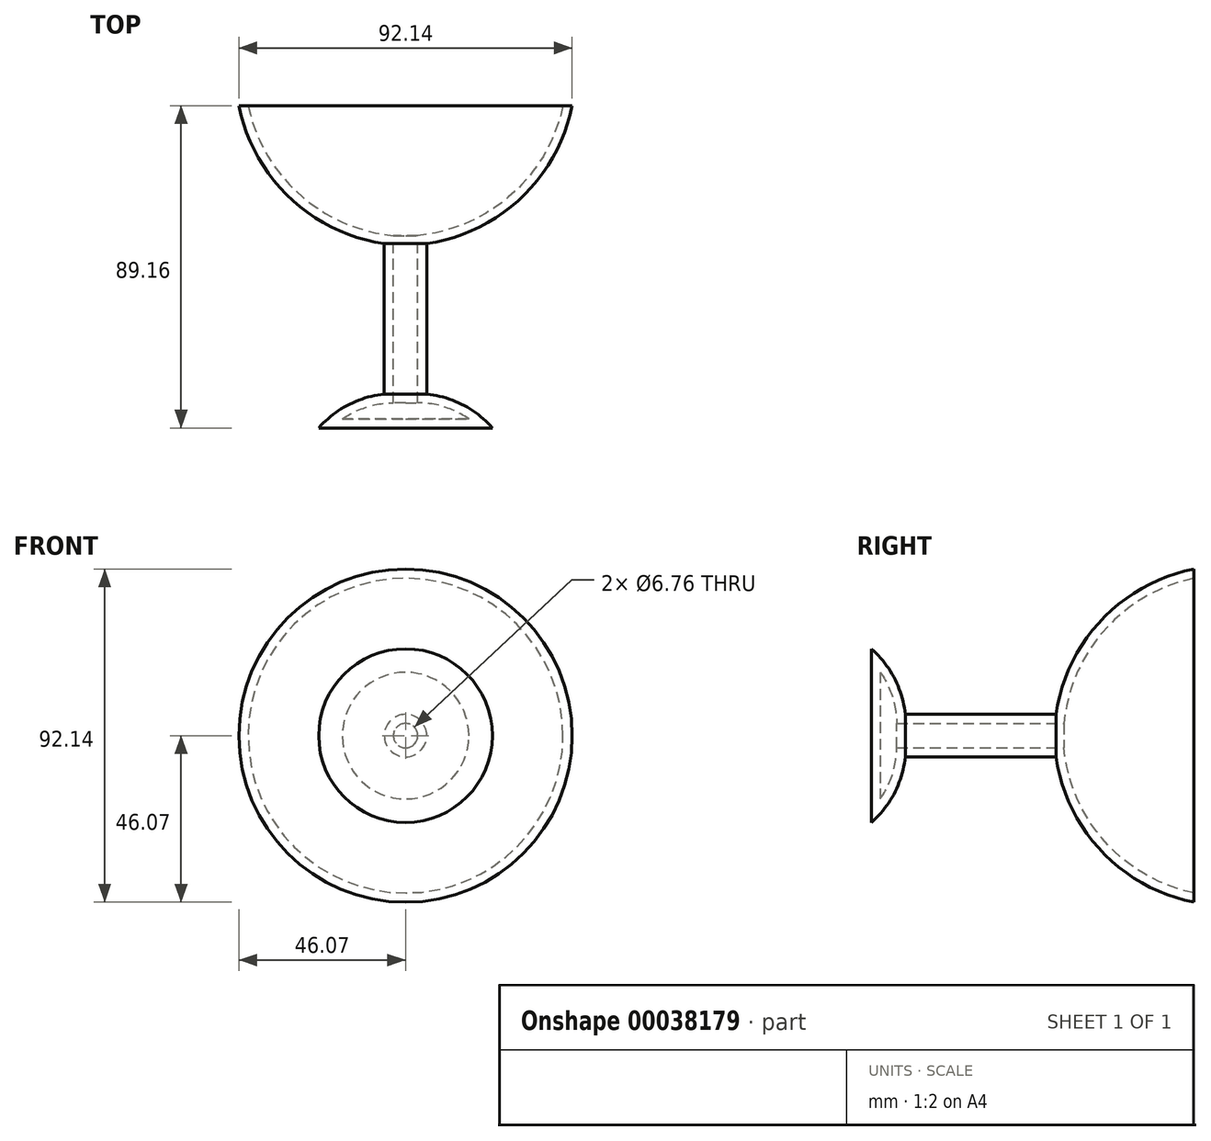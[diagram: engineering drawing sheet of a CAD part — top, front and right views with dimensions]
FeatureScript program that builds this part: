
annotation { "Feature Type Name" : "Feature", "Feature Type Description" : "" }
export const myFeature = defineFeature(function(context is Context, id is Id, definition is map)
    precondition{}
    {
        {
            var Q0;
            Q0=qCreatedBy(makeId("Top.planeOp"),FACE);
            var sketch = newSketch(context, id + "F0", { "sketchPlane" : qUnion([Q0])});
            skLineSegment(sketch, "E0", {"start": v(0, 40.65) * mm, "end": v(0, -48.5) * mm});
            skLineSegment(sketch, "E1", {"start": v(0, -48.5) * mm, "end": v(24.01, -48.5) * mm});
            skLineSegment(sketch, "E2", {"start": v(0, 40.65) * mm, "end": v(46.07, 40.65) * mm});
            skLineSegment(sketch, "E3", {"start": v(5.88, 2.52) * mm, "end": v(5.88, -39.14) * mm});
            skArc(sketch, "E4", {"start": v(5.88, 2.52) * mm, "mid": v(32.04, 15.2) * mm, "end": v(46.07, 40.65) * mm});
            skArc(sketch, "E5", {"start": v(24.01, -48.5) * mm, "mid": v(15.84, -42.1) * mm, "end": v(5.88, -39.14) * mm});
            skSolve(sketch);
        }
        {
            var Q0;
            Q0=makeQuery(id+"F0.imprint","IMPRINT",FACE,{"disambiguationData":[TD([[makeQuery(id+"F0.imprint","IMPRINT",EDGE,{"derivedFrom":sQuery(id+"F0.wireOp",EDGE,"E0")}),1.0]])]});
            var Q1;
            Q1=sQuery(id+"F0.wireOp",EDGE,"E0");
            revolve(context, id + "F1", {"entities" : qUnion([Q0]), "axis" : qUnion([Q1]), "revolveType" : RevolveType.FULL});
        }
        {
            var Q0;
            Q0=makeQuery(id+"F1.opRevolve","SWEPT_FACE",FACE,{"disambiguationData":[OSD([sQuery(id+"F0.wireOp",EDGE,"E2")])]});
            shell(context, id + "F2", {"entities" : qUnion([Q0]), "thickness" : 2.5 * mm});
        }
    });
